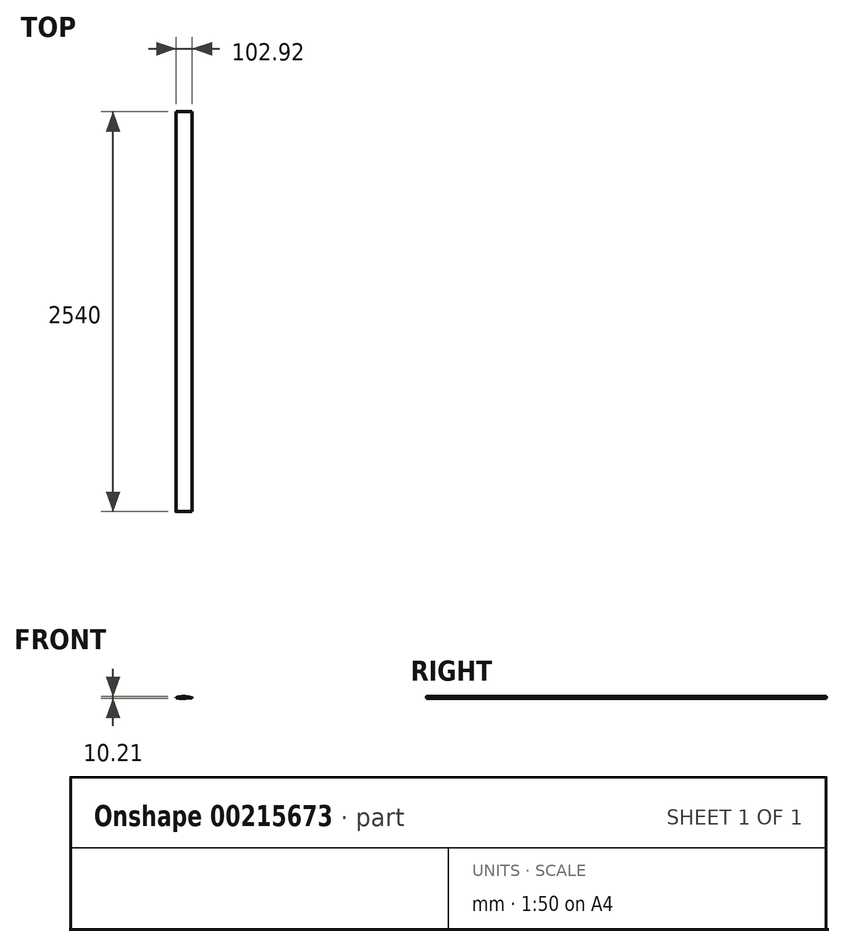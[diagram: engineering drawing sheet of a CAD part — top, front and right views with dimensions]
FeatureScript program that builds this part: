
annotation { "Feature Type Name" : "Feature", "Feature Type Description" : "" }
export const myFeature = defineFeature(function(context is Context, id is Id, definition is map)
    precondition{}
    {
        {
            var Q0;
            Q0=qCreatedBy(makeId("Front.planeOp"),FACE);
            var sketch = newSketch(context, id + "F0", { "sketchPlane" : qUnion([Q0])});
            skFitSpline(sketch, "E0", {"points": [v(-55.7, 24.68) * mm, v(-38, 30.83) * mm, v(13.79, 31.58) * mm, v(30.92, 28.22) * mm, v(38.93, 26.17) * mm, v(46.2, 24.87) * mm, v(-55.7, 24.68) * mm]});
            skSolve(sketch);
        }
        {
            var Q0;
            Q0 = qSketchRegion(id + "F0", true);
            extrude(context, id + "F1", {"entities" : qUnion([Q0]), "depth" : 2540 * mm});
        }
    });
